# Revit family: Toilet-Floor_Mount-KOHLER-WELLCOMME-K-96053LM_1
name_source: partatom
category: Plumbing Fixtures
revit_build: Autodesk Revit 2017 (Build: 20160225_1515(x64)
units: mm (PartAtom-declared; Revit-internal decimal feet)

## family parameters
Cut with Voids When Loaded = No
Host = Face
OmniClass Number = 23.31.19.17.11
OmniClass Title = Floor Mounted Toilets With Tank
Part Type = Normal
Room Calculation Point = No
Round Connector Dimension = Use Diameter
Shared = No

## types (1)
- Flushometer Bowl, 0-White
    ADA Compliant = No
    Assembly Code = D2010100
    CW Connection = Yes
    Cold Water Inlet = Cold Water Inlet
    Date Modified = 03/05/2021
    Default Elevation = 0"
    Description = Institutional toilet bowl with top connection for flushometer
    Finish = Kohler-Vitreous_China-0-White
    Flow Rate = 25 GPM
    Flush Rate = 1.6 GPF
    HW Connection = No
    Height = 15 1/4"
    Hot Water Inlet = Hot Water Inlet
    Length = 26 3/8"
    Manufacturer = KOHLER Co.
    Master Format 2014 Name = Residential Water Closets
    MasterFormat 2014 = 22 42 13.13
    Material = Vitreous China
    Model = K-96053LM-0
    Pressure = 80.00 psi
    Product Documentation Link = http://www.us.kohler.com
    Product Name = Wellcomme_Ultra
    Product Page URL = https://la.kohler.com
    Seat Included = No
    Type = 1
    URL = https://la.kohler.com
    Vent Connection = No
    Waste Connection = Yes
    Waste Water Outlet = Waste Water Outlet
    WaterSense Certified = Yes
    Width = 14 7/8"

## geometry (parser evidence)
native form markers: Sweep x4
no freeform markers — native parametric forms only
